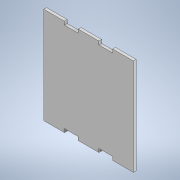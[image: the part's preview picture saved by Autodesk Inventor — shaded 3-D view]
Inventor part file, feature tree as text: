
AUTODESK INVENTOR PART (.ipt)
format: ipt  version: 2020.3 (Build 243373000, 373)  size: 126,464 bytes
history: native  units: mm
features: projected_geometry x5, sketch x2, extrude x1
ambient origin geometry x8: Origin, YZ Plane, XZ Plane, XY Plane, X Axis, Y Axis, Z Axis, Center Point
bodies: Solid1 (feature_tree)
feature tree (8):
  extrude  "Extrusion1"  [1 undecoded]
  sketch  "Sketch2"
  sketch  "Sketch1"  dims[d5=4.0mm d6=0.0mm]
  projected_geometry  "Projected Loop1"
  projected_geometry  "Projected Loop2"
  projected_geometry  "Projected Loop3"
  projected_geometry  "Projected Loop4"
  projected_geometry  "Projected Loop5"
note: 1 required parameter value undecoded (feature->parameter linkage not recoverable at this tier; creation-order binding heuristic only, values carry confidence <= 0.55)
